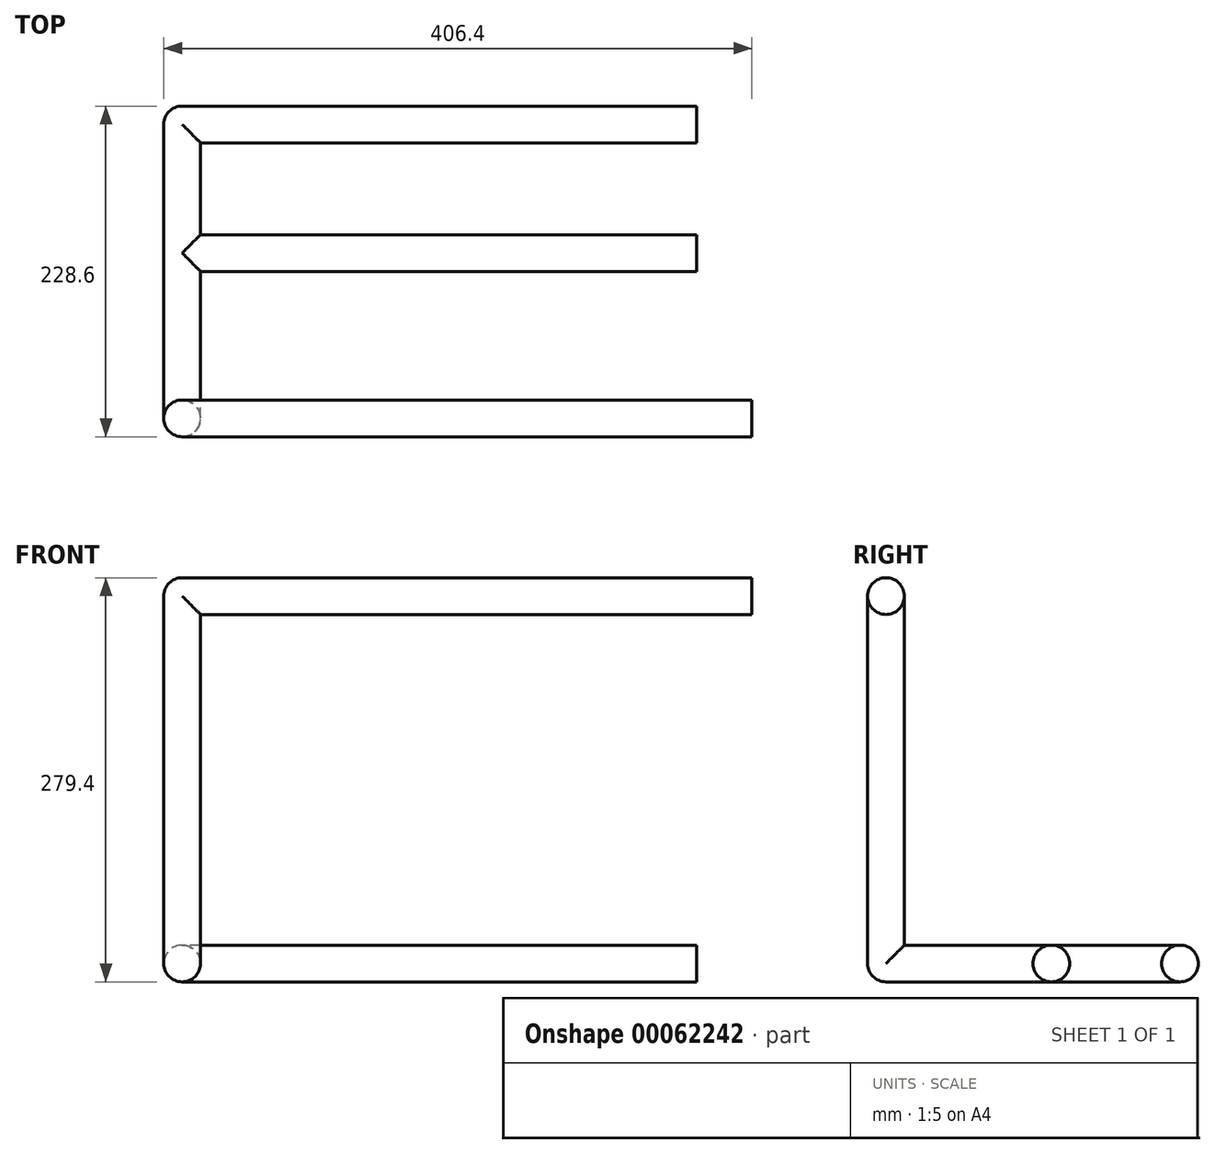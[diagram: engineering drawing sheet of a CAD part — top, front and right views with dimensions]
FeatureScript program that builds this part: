
annotation { "Feature Type Name" : "Feature", "Feature Type Description" : "" }
export const myFeature = defineFeature(function(context is Context, id is Id, definition is map)
    precondition{}
    {
        {
            var Q0;
            Q0=qCreatedBy(makeId("Top.planeOp"),FACE);
            var sketch = newSketch(context, id + "F0", { "sketchPlane" : qUnion([Q0])});
            skLineSegment(sketch, "E0.bottom", {"start": v(-203.2, 12.7) * mm, "end": v(203.2, 12.7) * mm});
            skLineSegment(sketch, "E0.top", {"start": v(-203.2, -12.7) * mm, "end": v(203.2, -12.7) * mm});
            skLineSegment(sketch, "E0.left", {"start": v(-203.2, 12.7) * mm, "end": v(-203.2, -12.7) * mm});
            skLineSegment(sketch, "E0.right", {"start": v(203.2, 12.7) * mm, "end": v(203.2, -12.7) * mm});
            skPoint(sketch, "E0.middle", {"position": v(0, 0) * mm});
            skSolve(sketch);
        }
        {
            var Q0;
            Q0 = qSketchRegion(id + "F0", true);
            extrude(context, id + "F1", {"entities" : qUnion([Q0]), "oppositeDirection" : true, "depth" : 25.4 * mm});
        }
        {
            var Q0;
            Q0=makeQuery(id+"F1.opExtrude","CAP_FACE",FACE,{"disambiguationData":[OSD([sQuery(id+"F0.wireOp",EDGE,"E0.bottom"),sQuery(id+"F0.wireOp",EDGE,"E0.top"),sQuery(id+"F0.wireOp",EDGE,"E0.left"),sQuery(id+"F0.wireOp",EDGE,"E0.right")])],"isStart":false});
            var sketch = newSketch(context, id + "F2", { "sketchPlane" : qUnion([Q0])});
            skLineSegment(sketch, "E1.bottom", {"start": v(-203.2, -12.7) * mm, "end": v(-177.8, -12.7) * mm});
            skLineSegment(sketch, "E1.top", {"start": v(-203.2, 12.7) * mm, "end": v(-177.8, 12.7) * mm});
            skLineSegment(sketch, "E1.left", {"start": v(-203.2, -12.7) * mm, "end": v(-203.2, 12.7) * mm});
            skLineSegment(sketch, "E1.right", {"start": v(-177.8, -12.7) * mm, "end": v(-177.8, 12.7) * mm});
            skSolve(sketch);
        }
        {
            var Q0;
            Q0 = qSketchRegion(id + "F2", true);
            extrude(context, id + "F3", {"entities" : qUnion([Q0]), "operationType" : NewBodyOperationType.ADD, "depth" : 228.6 * mm});
        }
        {
            var Q0;
            Q0=makeQuery(id+"F3.opExtrude","CAP_FACE",FACE,{"disambiguationData":[OSD([sQuery(id+"F2.wireOp",EDGE,"E1.bottom"),sQuery(id+"F2.wireOp",EDGE,"E1.top"),sQuery(id+"F2.wireOp",EDGE,"E1.left"),sQuery(id+"F2.wireOp",EDGE,"E1.right")])],"isStart":false});
            var sketch = newSketch(context, id + "F4", { "sketchPlane" : qUnion([Q0])});
            skLineSegment(sketch, "E2.bottom", {"start": v(-177.8, 12.7) * mm, "end": v(-203.2, 12.7) * mm});
            skLineSegment(sketch, "E2.top", {"start": v(-177.8, -215.9) * mm, "end": v(-203.2, -215.9) * mm});
            skLineSegment(sketch, "E2.left", {"start": v(-177.8, 12.7) * mm, "end": v(-177.8, -215.9) * mm});
            skLineSegment(sketch, "E2.right", {"start": v(-203.2, 12.7) * mm, "end": v(-203.2, -215.9) * mm});
            skSolve(sketch);
        }
        {
            var Q0;
            Q0 = qSketchRegion(id + "F4", true);
            extrude(context, id + "F5", {"entities" : qUnion([Q0]), "operationType" : NewBodyOperationType.ADD, "depth" : 25.4 * mm});
        }
        {
            var Q0;
            Q0=makeQuery(id+"F5.boolean.opBoolean","MERGE",FACE,{"derivedFrom":[makeQuery(id+"F3.opExtrude","SWEPT_FACE",FACE,{"disambiguationData":[OSD([sQuery(id+"F2.wireOp",EDGE,"E1.right")])]}),makeQuery(id+"F5.opExtrude","SWEPT_FACE",FACE,{"disambiguationData":[OSD([sQuery(id+"F4.wireOp",EDGE,"E2.left")])]})]});
            var sketch = newSketch(context, id + "F6", { "sketchPlane" : qUnion([Q0])});
            skLineSegment(sketch, "E3.bottom", {"start": v(215.9, -279.4) * mm, "end": v(190.5, -279.4) * mm});
            skLineSegment(sketch, "E3.top", {"start": v(215.9, -254) * mm, "end": v(190.5, -254) * mm});
            skLineSegment(sketch, "E3.left", {"start": v(215.9, -279.4) * mm, "end": v(215.9, -254) * mm});
            skLineSegment(sketch, "E3.right", {"start": v(190.5, -279.4) * mm, "end": v(190.5, -254) * mm});
            skLineSegment(sketch, "E4.bottom", {"start": v(127, -279.4) * mm, "end": v(101.6, -279.4) * mm});
            skLineSegment(sketch, "E4.top", {"start": v(127, -254) * mm, "end": v(101.6, -254) * mm});
            skLineSegment(sketch, "E4.left", {"start": v(127, -279.4) * mm, "end": v(127, -254) * mm});
            skLineSegment(sketch, "E4.right", {"start": v(101.6, -279.4) * mm, "end": v(101.6, -254) * mm});
            skSolve(sketch);
        }
        {
            var Q0;
            Q0 = qSketchRegion(id + "F6", true);
            extrude(context, id + "F7", {"entities" : qUnion([Q0]), "operationType" : NewBodyOperationType.ADD, "depth" : 342.9 * mm});
        }
        {
            var Q0;
            Q0=makeQuery(id+"F7.boolean.opBoolean","MERGE",EDGE,{"derivedFrom":[makeQuery(id+"F5.opExtrude","CAP_EDGE",EDGE,{"disambiguationData":[OSD([sQuery(id+"F4.wireOp",EDGE,"E2.top")])],"isStart":false}),makeQuery(id+"F7.opExtrude","SWEPT_EDGE",EDGE,{"disambiguationData":[OSD([sQuery(id+"F6.wireOp",EDGE,"E3.bottom"),sQuery(id+"F6.wireOp",EDGE,"E3.left")])]})]});
            var Q1;
            Q1=makeQuery(id+"F5.opExtrude","SWEPT_EDGE",EDGE,{"disambiguationData":[OSD([sQuery(id+"F4.wireOp",EDGE,"E2.top"),sQuery(id+"F4.wireOp",EDGE,"E2.right")])]});
            var Q2;
            Q2=makeQuery(id+"F7.opExtrude","SWEPT_EDGE",EDGE,{"disambiguationData":[OSD([sQuery(id+"F4.wireOp",EDGE,"E2.left"),sQuery(id+"F6.wireOp",EDGE,"E3.bottom"),sQuery(id+"F6.wireOp",EDGE,"E3.right")])]});
            var Q3;
            {var subQ0=sQuery(id+"F4.wireOp",EDGE,"E2.left");Q3=makeQuery(id+"F7.boolean.opBoolean","SPLIT",EDGE,{"disambiguationData":[TD([makeQuery(id+"F7.opExtrude","SWEPT_FACE",FACE,{"disambiguationData":[OSD([sQuery(id+"F6.wireOp",EDGE,"E3.right")])]})])],"derivedFrom":makeQuery(id+"F5.opExtrude","CAP_EDGE",EDGE,{"disambiguationData":[OSD([subQ0])],"isStart":false})});}
            var Q4;
            Q4=makeQuery(id+"F5.opExtrude","CAP_EDGE",EDGE,{"disambiguationData":[OSD([sQuery(id+"F4.wireOp",EDGE,"E2.right")])],"isStart":false});
            var Q5;
            Q5=makeQuery(id+"F7.opExtrude","SWEPT_EDGE",EDGE,{"disambiguationData":[OSD([sQuery(id+"F4.wireOp",EDGE,"E2.left"),sQuery(id+"F6.wireOp",EDGE,"E4.bottom"),sQuery(id+"F6.wireOp",EDGE,"E4.left")])]});
            var Q6;
            Q6=makeQuery(id+"F7.opExtrude","SWEPT_EDGE",EDGE,{"disambiguationData":[OSD([sQuery(id+"F4.wireOp",EDGE,"E2.left"),sQuery(id+"F6.wireOp",EDGE,"E4.bottom"),sQuery(id+"F6.wireOp",EDGE,"E4.right")])]});
            var Q7;
            {var subQ1=sQuery(id+"F4.wireOp",EDGE,"E2.left");Q7=makeQuery(id+"F7.boolean.opBoolean","SPLIT",EDGE,{"disambiguationData":[TD([makeQuery(id+"F1.opExtrude","SWEPT_FACE",FACE,{"disambiguationData":[OSD([sQuery(id+"F0.wireOp",EDGE,"E0.top")])]})])],"derivedFrom":makeQuery(id+"F5.opExtrude","CAP_EDGE",EDGE,{"disambiguationData":[OSD([subQ1])],"isStart":false})});}
            var Q8;
            Q8=makeQuery(id+"F5.opExtrude","CAP_EDGE",EDGE,{"disambiguationData":[OSD([sQuery(id+"F4.wireOp",EDGE,"E2.bottom")])],"isStart":false});
            var Q9;
            Q9=makeQuery(id+"F1.opExtrude","CAP_EDGE",EDGE,{"disambiguationData":[OSD([sQuery(id+"F0.wireOp",EDGE,"E0.left")])],"isStart":true});
            var Q10;
            Q10=makeQuery(id+"F5.boolean.opBoolean","MERGE",EDGE,{"derivedFrom":[makeQuery(id+"F3.boolean.opBoolean","MERGE",EDGE,{"derivedFrom":[makeQuery(id+"F1.opExtrude","SWEPT_EDGE",EDGE,{"disambiguationData":[OSD([sQuery(id+"F0.wireOp",EDGE,"E0.top"),sQuery(id+"F0.wireOp",EDGE,"E0.left")])]}),makeQuery(id+"F3.opExtrude","SWEPT_EDGE",EDGE,{"disambiguationData":[OSD([sQuery(id+"F2.wireOp",EDGE,"E1.top"),sQuery(id+"F2.wireOp",EDGE,"E1.left")])]})]}),makeQuery(id+"F5.opExtrude","SWEPT_EDGE",EDGE,{"disambiguationData":[OSD([sQuery(id+"F4.wireOp",EDGE,"E2.bottom"),sQuery(id+"F4.wireOp",EDGE,"E2.right")])]})]});
            var Q11;
            Q11=makeQuery(id+"F3.boolean.opBoolean","MERGE",EDGE,{"derivedFrom":[makeQuery(id+"F1.opExtrude","SWEPT_EDGE",EDGE,{"disambiguationData":[OSD([sQuery(id+"F0.wireOp",EDGE,"E0.bottom"),sQuery(id+"F0.wireOp",EDGE,"E0.left")])]}),makeQuery(id+"F3.opExtrude","SWEPT_EDGE",EDGE,{"disambiguationData":[OSD([sQuery(id+"F2.wireOp",EDGE,"E1.bottom"),sQuery(id+"F2.wireOp",EDGE,"E1.left")])]})]});
            var Q12;
            Q12=makeQuery(id+"F1.opExtrude","CAP_EDGE",EDGE,{"disambiguationData":[OSD([sQuery(id+"F0.wireOp",EDGE,"E0.bottom")])],"isStart":false});
            var Q13;
            Q13=makeQuery(id+"F1.opExtrude","CAP_EDGE",EDGE,{"disambiguationData":[OSD([sQuery(id+"F0.wireOp",EDGE,"E0.top")])],"isStart":false});
            var Q14;
            Q14=makeQuery(id+"F7.opExtrude","SWEPT_EDGE",EDGE,{"disambiguationData":[OSD([sQuery(id+"F4.wireOp",EDGE,"E2.left"),sQuery(id+"F6.wireOp",EDGE,"E3.top"),sQuery(id+"F6.wireOp",EDGE,"E3.right")])]});
            var Q15;
            Q15=makeQuery(id+"F7.opExtrude","SWEPT_EDGE",EDGE,{"disambiguationData":[OSD([sQuery(id+"F4.wireOp",EDGE,"E2.left"),sQuery(id+"F6.wireOp",EDGE,"E4.top"),sQuery(id+"F6.wireOp",EDGE,"E4.right")])]});
            var Q16;
            Q16=makeQuery(id+"F1.opExtrude","CAP_EDGE",EDGE,{"disambiguationData":[OSD([sQuery(id+"F0.wireOp",EDGE,"E0.top")])],"isStart":true});
            var Q17;
            Q17=makeQuery(id+"F1.opExtrude","CAP_EDGE",EDGE,{"disambiguationData":[OSD([sQuery(id+"F0.wireOp",EDGE,"E0.bottom")])],"isStart":true});
            var Q18;
            Q18=makeQuery(id+"F3.opExtrude","SWEPT_EDGE",EDGE,{"disambiguationData":[OSD([sQuery(id+"F0.wireOp",EDGE,"E0.bottom"),sQuery(id+"F2.wireOp",EDGE,"E1.bottom"),sQuery(id+"F2.wireOp",EDGE,"E1.right")])]});
            var Q19;
            Q19=makeQuery(id+"F7.opExtrude","SWEPT_EDGE",EDGE,{"disambiguationData":[OSD([sQuery(id+"F4.wireOp",EDGE,"E2.left"),sQuery(id+"F6.wireOp",EDGE,"E4.top"),sQuery(id+"F6.wireOp",EDGE,"E4.left")])]});
            var Q20;
            Q20=makeQuery(id+"F7.boolean.opBoolean","MERGE",EDGE,{"derivedFrom":[makeQuery(id+"F5.opExtrude","CAP_EDGE",EDGE,{"disambiguationData":[OSD([sQuery(id+"F4.wireOp",EDGE,"E2.top")])],"isStart":true}),makeQuery(id+"F7.opExtrude","SWEPT_EDGE",EDGE,{"disambiguationData":[OSD([sQuery(id+"F6.wireOp",EDGE,"E3.top"),sQuery(id+"F6.wireOp",EDGE,"E3.left")])]})]});
            var Q21;
            {var subQ0=sQuery(id+"F4.wireOp",EDGE,"E2.left");Q21=makeQuery(id+"F7.boolean.opBoolean","SPLIT",EDGE,{"disambiguationData":[TD([makeQuery(id+"F1.opExtrude","SWEPT_FACE",FACE,{"disambiguationData":[OSD([sQuery(id+"F0.wireOp",EDGE,"E0.bottom")])]})])],"derivedFrom":makeQuery(id+"F5.opExtrude","CAP_EDGE",EDGE,{"disambiguationData":[OSD([subQ0])],"isStart":true})});}
            var Q22;
            {var subQ0=sQuery(id+"F4.wireOp",EDGE,"E2.left");Q22=makeQuery(id+"F7.boolean.opBoolean","SPLIT",EDGE,{"disambiguationData":[TD([makeQuery(id+"F7.opExtrude","SWEPT_FACE",FACE,{"disambiguationData":[OSD([sQuery(id+"F6.wireOp",EDGE,"E3.right")])]})])],"derivedFrom":makeQuery(id+"F5.opExtrude","CAP_EDGE",EDGE,{"disambiguationData":[OSD([subQ0])],"isStart":true})});}
            var Q23;
            Q23=makeQuery(id+"F5.boolean.opBoolean","MERGE",EDGE,{"derivedFrom":[makeQuery(id+"F3.opExtrude","SWEPT_EDGE",EDGE,{"disambiguationData":[OSD([sQuery(id+"F0.wireOp",EDGE,"E0.top"),sQuery(id+"F2.wireOp",EDGE,"E1.top"),sQuery(id+"F2.wireOp",EDGE,"E1.right")])]}),makeQuery(id+"F5.opExtrude","SWEPT_EDGE",EDGE,{"disambiguationData":[OSD([sQuery(id+"F4.wireOp",EDGE,"E2.bottom"),sQuery(id+"F4.wireOp",EDGE,"E2.left")])]})]});
            var Q24;
            Q24=makeQuery(id+"F5.opExtrude","CAP_EDGE",EDGE,{"disambiguationData":[OSD([sQuery(id+"F4.wireOp",EDGE,"E2.right")])],"isStart":true});
            fillet(context, id + "F8", {"entities" : qUnion([Q0, Q1, Q2, Q3, Q4, Q5, Q6, Q7, Q8, Q9, Q10, Q11, Q12, Q13, Q14, Q15, Q16, Q17, Q18, Q19, Q20, Q21, Q22, Q23, Q24]), "radius" : 12.7 * mm, "tangentPropagation" : true, "allowEdgeOverflow" : false});
        }
    });
